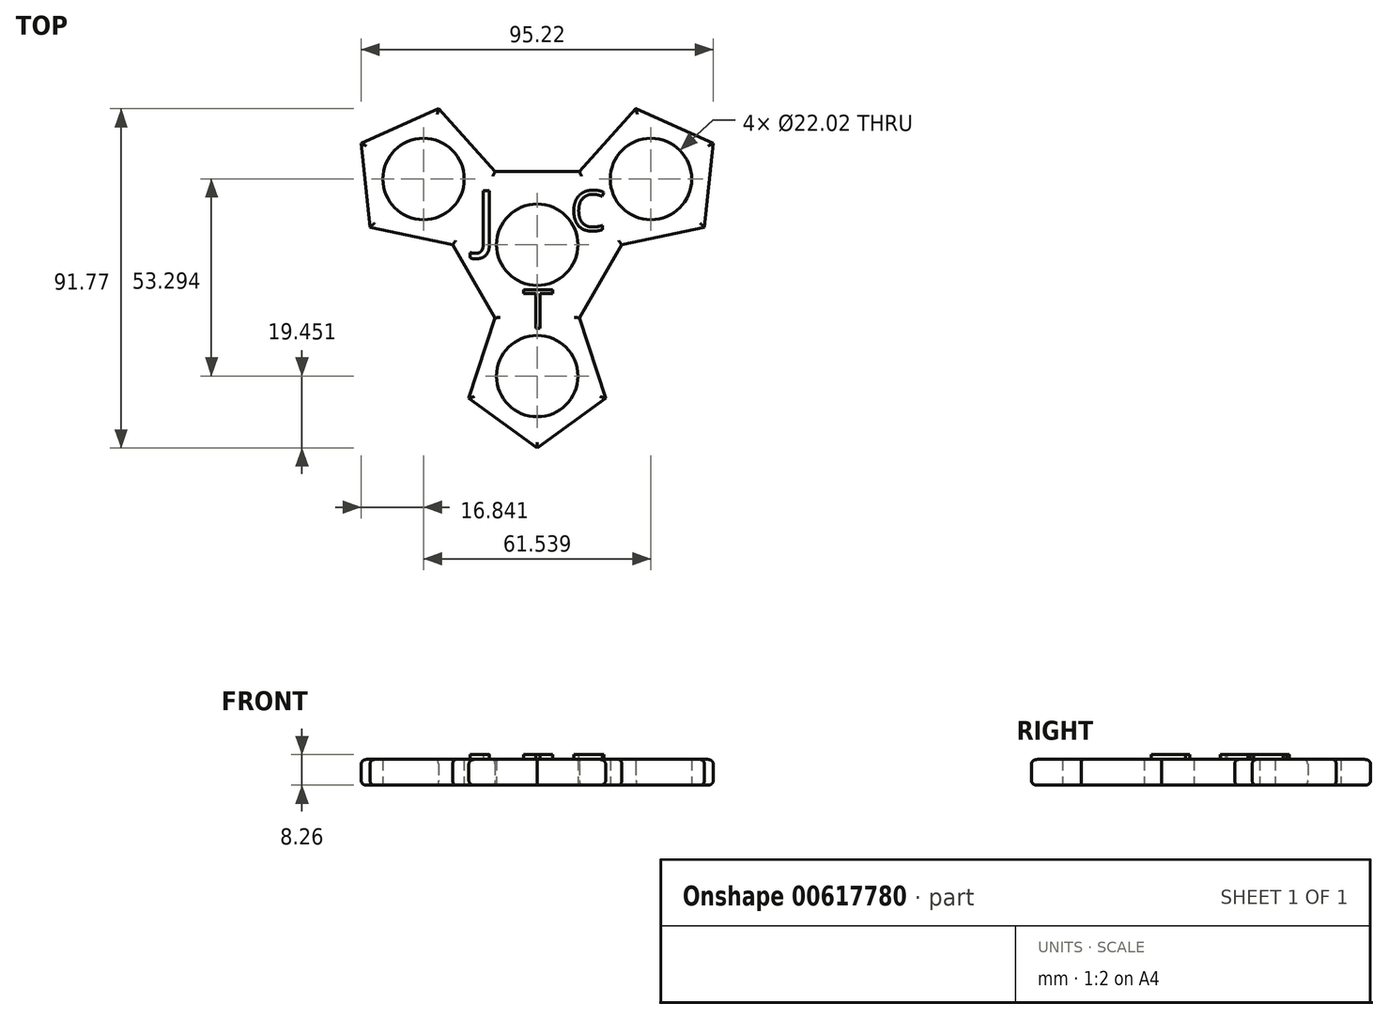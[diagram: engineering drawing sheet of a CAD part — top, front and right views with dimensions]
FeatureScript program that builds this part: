
annotation { "Feature Type Name" : "Feature", "Feature Type Description" : "" }
export const myFeature = defineFeature(function(context is Context, id is Id, definition is map)
    precondition{}
    {
        {
            var Q0;
            Q0=qCreatedBy(makeId("Top.planeOp"),FACE);
            var sketch = newSketch(context, id + "F0", { "sketchPlane" : qUnion([Q0])});
            skCircle(sketch, "E0", {"center": v(0, 0) * mm, "radius": 11.01 * mm});
            skLineSegment(sketch, "E1", {"start": v(0, 0) * mm, "end": v(-30.77, 17.76) * mm});
            skLineSegment(sketch, "E2", {"start": v(0, 0) * mm, "end": v(30.77, 17.76) * mm});
            skLineSegment(sketch, "E3", {"start": v(0, 0) * mm, "end": v(0, -35.53) * mm});
            skCircle(sketch, "E4", {"center": v(-30.77, 17.76) * mm, "radius": 11.01 * mm});
            skCircle(sketch, "E5", {"center": v(30.77, 17.76) * mm, "radius": 11.01 * mm});
            skCircle(sketch, "E6", {"center": v(0, -35.53) * mm, "radius": 11.01 * mm});
            skCircle(sketch, "E7.cCircle", {"center": v(-30.77, 17.76) * mm, "radius": 19.45 * mm, "construction": true});
            skLineSegment(sketch, "E7.0", {"start": v(-11.43, 19.8) * mm, "end": v(-22.86, 0) * mm});
            skLineSegment(sketch, "E7.1", {"start": v(-22.86, 0) * mm, "end": v(-45.22, 4.75) * mm});
            skLineSegment(sketch, "E7.2", {"start": v(-45.22, 4.75) * mm, "end": v(-47.6, 27.49) * mm});
            skLineSegment(sketch, "E7.3", {"start": v(-47.6, 27.49) * mm, "end": v(-26.73, 36.79) * mm});
            skLineSegment(sketch, "E7.4", {"start": v(-26.73, 36.79) * mm, "end": v(-11.43, 19.8) * mm});
            skCircle(sketch, "E8.cCircle", {"center": v(30.77, 17.76) * mm, "radius": 19.45 * mm, "construction": true});
            skLineSegment(sketch, "E8.0", {"start": v(11.43, 19.8) * mm, "end": v(26.73, 36.79) * mm});
            skLineSegment(sketch, "E8.1", {"start": v(26.73, 36.79) * mm, "end": v(47.6, 27.49) * mm});
            skLineSegment(sketch, "E8.2", {"start": v(47.6, 27.49) * mm, "end": v(45.22, 4.75) * mm});
            skLineSegment(sketch, "E8.3", {"start": v(45.22, 4.75) * mm, "end": v(22.86, 0) * mm});
            skLineSegment(sketch, "E8.4", {"start": v(22.86, 0) * mm, "end": v(11.43, 19.8) * mm});
            skCircle(sketch, "E9.cCircle", {"center": v(0, -35.53) * mm, "radius": 19.45 * mm, "construction": true});
            skLineSegment(sketch, "E9.0", {"start": v(18.5, -41.54) * mm, "end": v(0, -54.98) * mm});
            skLineSegment(sketch, "E9.1", {"start": v(0, -54.98) * mm, "end": v(-18.5, -41.54) * mm});
            skLineSegment(sketch, "E9.2", {"start": v(-18.5, -41.54) * mm, "end": v(-11.43, -19.8) * mm});
            skLineSegment(sketch, "E9.3", {"start": v(-11.43, -19.8) * mm, "end": v(11.43, -19.8) * mm});
            skLineSegment(sketch, "E9.4", {"start": v(11.43, -19.8) * mm, "end": v(18.5, -41.54) * mm});
            skCircle(sketch, "E10.cCircle", {"center": v(0, 0) * mm, "radius": 22.86 * mm, "construction": true});
            skLineSegment(sketch, "E10.0", {"start": v(11.43, -19.8) * mm, "end": v(-11.43, -19.8) * mm});
            skLineSegment(sketch, "E10.1", {"start": v(-11.43, -19.8) * mm, "end": v(-22.86, 0) * mm});
            skLineSegment(sketch, "E10.2", {"start": v(-22.86, 0) * mm, "end": v(-11.43, 19.8) * mm});
            skLineSegment(sketch, "E10.3", {"start": v(-11.43, 19.8) * mm, "end": v(11.43, 19.8) * mm});
            skLineSegment(sketch, "E10.4", {"start": v(11.43, 19.8) * mm, "end": v(22.86, 0) * mm});
            skLineSegment(sketch, "E10.5", {"start": v(22.86, 0) * mm, "end": v(11.43, -19.8) * mm});
            skSolve(sketch);
        }
        {
            var Q0;
            Q0 = qSketchRegion(id + "F0", true);
            extrude(context, id + "F1", {"entities" : qUnion([Q0]), "depth" : 7 * mm, "offsetDistance" : 25.4 * mm});
        }
        {
            var Q0;
            Q0=makeQuery(id+"F1.opExtrude","CAP_FACE",FACE,{"disambiguationData":[OSD([sQuery(id+"F0.wireOp",EDGE,"E0"),sQuery(id+"F0.wireOp",EDGE,"E4"),sQuery(id+"F0.wireOp",EDGE,"E5"),sQuery(id+"F0.wireOp",EDGE,"E6"),sQuery(id+"F0.wireOp",EDGE,"E7.1"),sQuery(id+"F0.wireOp",EDGE,"E7.2"),sQuery(id+"F0.wireOp",EDGE,"E7.3"),sQuery(id+"F0.wireOp",EDGE,"E7.4"),sQuery(id+"F0.wireOp",EDGE,"E8.0"),sQuery(id+"F0.wireOp",EDGE,"E8.1"),sQuery(id+"F0.wireOp",EDGE,"E8.2"),sQuery(id+"F0.wireOp",EDGE,"E8.3"),sQuery(id+"F0.wireOp",EDGE,"E9.0"),sQuery(id+"F0.wireOp",EDGE,"E9.1"),sQuery(id+"F0.wireOp",EDGE,"E9.2"),sQuery(id+"F0.wireOp",EDGE,"E9.4"),sQuery(id+"F0.wireOp",EDGE,"E10.1"),sQuery(id+"F0.wireOp",EDGE,"E10.3"),sQuery(id+"F0.wireOp",EDGE,"E10.5")])],"isStart":false});
            var sketch = newSketch(context, id + "F2", { "sketchPlane" : qUnion([Q0])});
            skText(sketch, "E11", { "text": "J", "fontName": "OpenSans-Regular.ttf"});
            skText(sketch, "E12", { "text": "C", "fontName": "OpenSans-Regular.ttf"});
            skText(sketch, "E13", { "text": "T", "fontName": "OpenSans-Regular.ttf"});
            skPoint(sketch, "E14", {"position": v(-10, 7.36) * mm});
            const initialGuessF2  = {"E11": [-0.01651, 0, 1, 0, 0.01472], "E12": [0.00896, 0.00381, 1, 0, 0.0109], "E13": [-0.00384, -0.02261, 1, 0, 0.01055]};
            skSetInitialGuess(sketch, initialGuessF2);
            skSolve(sketch);
        }
        {
            var Q0;
            Q0 = qSketchRegion(id + "F2", true);
            extrude(context, id + "F3", {"entities" : qUnion([Q0]), "operationType" : NewBodyOperationType.ADD, "depth" : 1.27 * mm, "offsetDistance" : 25.4 * mm});
        }
        {
            var Q0;
            Q0=makeQuery(id+"F1.opExtrude","CAP_EDGE",EDGE,{"disambiguationData":[OSD([sQuery(id+"F0.wireOp",EDGE,"E10.3")])],"isStart":false});
            var Q1;
            Q1=makeQuery(id+"F1.opExtrude","CAP_EDGE",EDGE,{"disambiguationData":[OSD([sQuery(id+"F0.wireOp",EDGE,"E8.0")])],"isStart":false});
            var Q2;
            Q2=makeQuery(id+"F1.opExtrude","CAP_EDGE",EDGE,{"disambiguationData":[OSD([sQuery(id+"F0.wireOp",EDGE,"E9.4")])],"isStart":false});
            var Q3;
            Q3=makeQuery(id+"F1.opExtrude","CAP_EDGE",EDGE,{"disambiguationData":[OSD([sQuery(id+"F0.wireOp",EDGE,"E9.0")])],"isStart":false});
            var Q4;
            Q4=makeQuery(id+"F1.opExtrude","CAP_EDGE",EDGE,{"disambiguationData":[OSD([sQuery(id+"F0.wireOp",EDGE,"E9.1")])],"isStart":false});
            var Q5;
            Q5=makeQuery(id+"F1.opExtrude","CAP_EDGE",EDGE,{"disambiguationData":[OSD([sQuery(id+"F0.wireOp",EDGE,"E9.2")])],"isStart":false});
            var Q6;
            Q6=makeQuery(id+"F1.opExtrude","CAP_EDGE",EDGE,{"disambiguationData":[OSD([sQuery(id+"F0.wireOp",EDGE,"E10.5")])],"isStart":false});
            var Q7;
            Q7=makeQuery(id+"F1.opExtrude","CAP_EDGE",EDGE,{"disambiguationData":[OSD([sQuery(id+"F0.wireOp",EDGE,"E8.3")])],"isStart":false});
            var Q8;
            Q8=makeQuery(id+"F1.opExtrude","CAP_EDGE",EDGE,{"disambiguationData":[OSD([sQuery(id+"F0.wireOp",EDGE,"E8.2")])],"isStart":false});
            var Q9;
            Q9=makeQuery(id+"F1.opExtrude","CAP_EDGE",EDGE,{"disambiguationData":[OSD([sQuery(id+"F0.wireOp",EDGE,"E8.1")])],"isStart":false});
            var Q10;
            Q10=makeQuery(id+"F1.opExtrude","CAP_EDGE",EDGE,{"disambiguationData":[OSD([sQuery(id+"F0.wireOp",EDGE,"E7.4")])],"isStart":false});
            var Q11;
            Q11=makeQuery(id+"F1.opExtrude","CAP_EDGE",EDGE,{"disambiguationData":[OSD([sQuery(id+"F0.wireOp",EDGE,"E7.3")])],"isStart":false});
            var Q12;
            Q12=makeQuery(id+"F1.opExtrude","CAP_EDGE",EDGE,{"disambiguationData":[OSD([sQuery(id+"F0.wireOp",EDGE,"E7.2")])],"isStart":false});
            var Q13;
            Q13=makeQuery(id+"F1.opExtrude","CAP_EDGE",EDGE,{"disambiguationData":[OSD([sQuery(id+"F0.wireOp",EDGE,"E7.1")])],"isStart":false});
            var Q14;
            Q14=makeQuery(id+"F1.opExtrude","CAP_EDGE",EDGE,{"disambiguationData":[OSD([sQuery(id+"F0.wireOp",EDGE,"E10.1")])],"isStart":false});
            var Q15;
            Q15=makeQuery(id+"F1.opExtrude","CAP_EDGE",EDGE,{"disambiguationData":[OSD([sQuery(id+"F0.wireOp",EDGE,"E10.3")])],"isStart":true});
            var Q16;
            Q16=makeQuery(id+"F1.opExtrude","CAP_EDGE",EDGE,{"disambiguationData":[OSD([sQuery(id+"F0.wireOp",EDGE,"E7.4")])],"isStart":true});
            var Q17;
            Q17=makeQuery(id+"F1.opExtrude","CAP_EDGE",EDGE,{"disambiguationData":[OSD([sQuery(id+"F0.wireOp",EDGE,"E7.3")])],"isStart":true});
            var Q18;
            Q18=makeQuery(id+"F1.opExtrude","CAP_EDGE",EDGE,{"disambiguationData":[OSD([sQuery(id+"F0.wireOp",EDGE,"E7.2")])],"isStart":true});
            var Q19;
            Q19=makeQuery(id+"F1.opExtrude","CAP_EDGE",EDGE,{"disambiguationData":[OSD([sQuery(id+"F0.wireOp",EDGE,"E7.1")])],"isStart":true});
            var Q20;
            Q20=makeQuery(id+"F1.opExtrude","CAP_EDGE",EDGE,{"disambiguationData":[OSD([sQuery(id+"F0.wireOp",EDGE,"E10.1")])],"isStart":true});
            var Q21;
            Q21=makeQuery(id+"F1.opExtrude","CAP_EDGE",EDGE,{"disambiguationData":[OSD([sQuery(id+"F0.wireOp",EDGE,"E9.2")])],"isStart":true});
            var Q22;
            Q22=makeQuery(id+"F1.opExtrude","CAP_EDGE",EDGE,{"disambiguationData":[OSD([sQuery(id+"F0.wireOp",EDGE,"E9.1")])],"isStart":true});
            var Q23;
            Q23=makeQuery(id+"F1.opExtrude","CAP_EDGE",EDGE,{"disambiguationData":[OSD([sQuery(id+"F0.wireOp",EDGE,"E9.0")])],"isStart":true});
            var Q24;
            Q24=makeQuery(id+"F1.opExtrude","CAP_EDGE",EDGE,{"disambiguationData":[OSD([sQuery(id+"F0.wireOp",EDGE,"E9.4")])],"isStart":true});
            var Q25;
            Q25=makeQuery(id+"F1.opExtrude","CAP_EDGE",EDGE,{"disambiguationData":[OSD([sQuery(id+"F0.wireOp",EDGE,"E10.5")])],"isStart":true});
            var Q26;
            Q26=makeQuery(id+"F1.opExtrude","CAP_EDGE",EDGE,{"disambiguationData":[OSD([sQuery(id+"F0.wireOp",EDGE,"E8.3")])],"isStart":true});
            var Q27;
            Q27=makeQuery(id+"F1.opExtrude","CAP_EDGE",EDGE,{"disambiguationData":[OSD([sQuery(id+"F0.wireOp",EDGE,"E8.2")])],"isStart":true});
            var Q28;
            Q28=makeQuery(id+"F1.opExtrude","CAP_EDGE",EDGE,{"disambiguationData":[OSD([sQuery(id+"F0.wireOp",EDGE,"E8.1")])],"isStart":true});
            var Q29;
            Q29=makeQuery(id+"F1.opExtrude","CAP_EDGE",EDGE,{"disambiguationData":[OSD([sQuery(id+"F0.wireOp",EDGE,"E8.0")])],"isStart":true});
            fillet(context, id + "F4", {"entities" : qUnion([Q0, Q1, Q2, Q3, Q4, Q5, Q6, Q7, Q8, Q9, Q10, Q11, Q12, Q13, Q14, Q15, Q16, Q17, Q18, Q19, Q20, Q21, Q22, Q23, Q24, Q25, Q26, Q27, Q28, Q29]), "radius" : 1.27 * mm, "tangentPropagation" : true, "allowEdgeOverflow" : false});
        }
    });
